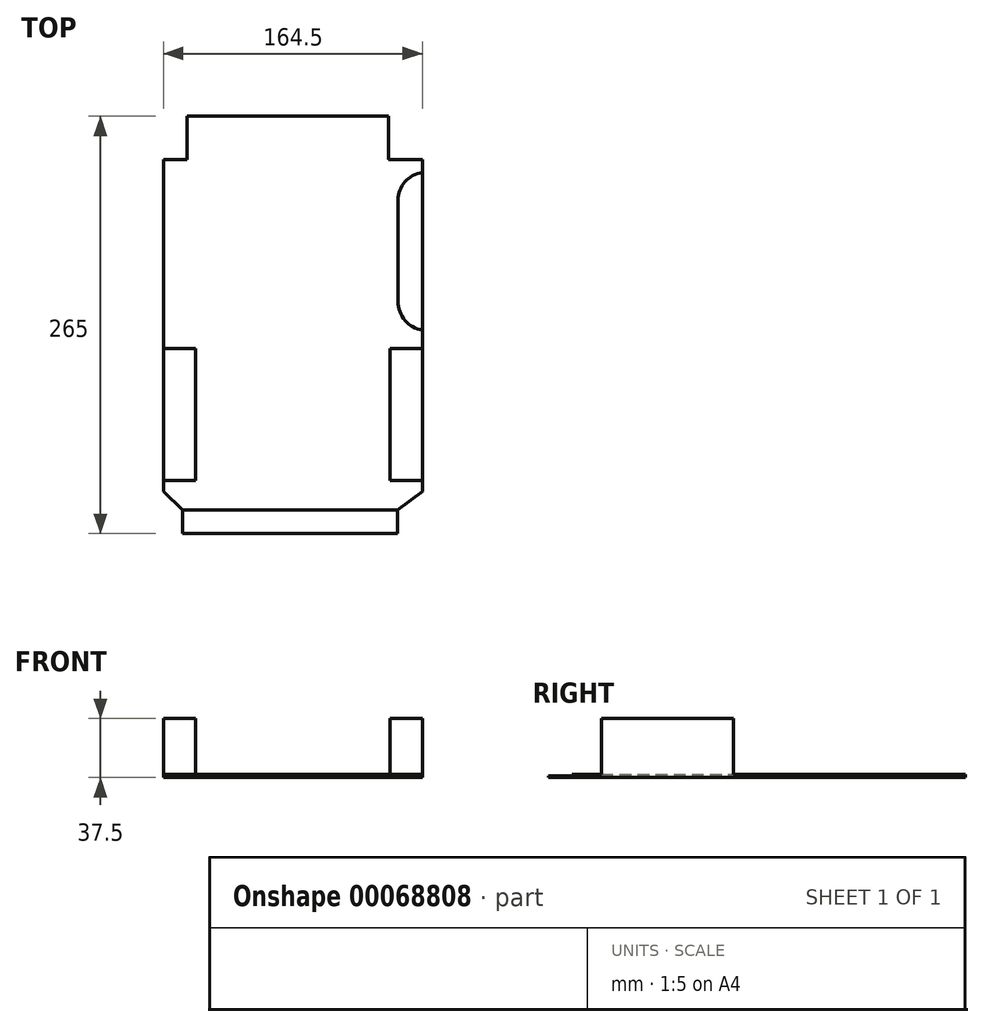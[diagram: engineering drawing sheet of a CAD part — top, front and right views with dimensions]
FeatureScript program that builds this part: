
annotation { "Feature Type Name" : "Feature", "Feature Type Description" : "" }
export const myFeature = defineFeature(function(context is Context, id is Id, definition is map)
    precondition{}
    {
        {
            var Q0;
            Q0=qCreatedBy(makeId("Top.planeOp"),FACE);
            var sketch = newSketch(context, id + "F0", { "sketchPlane" : qUnion([Q0])});
            skLineSegment(sketch, "E0", {"start": v(0, 0) * mm, "end": v(84.75, 0) * mm});
            skLineSegment(sketch, "E1", {"start": v(84.75, 0) * mm, "end": v(84.75, 15) * mm});
            skLineSegment(sketch, "E2", {"start": v(84.75, 15) * mm, "end": v(100.6, 26.65) * mm});
            skLineSegment(sketch, "E3", {"start": v(100.6, 26.65) * mm, "end": v(100.6, 33.65) * mm});
            skLineSegment(sketch, "E4", {"start": v(100.6, 33.65) * mm, "end": v(80.1, 33.65) * mm});
            skLineSegment(sketch, "E5", {"start": v(80.1, 33.65) * mm, "end": v(80.1, 117.65) * mm});
            skLineSegment(sketch, "E6", {"start": v(80.1, 117.65) * mm, "end": v(100.6, 117.65) * mm});
            skLineSegment(sketch, "E7", {"start": v(100.6, 117.65) * mm, "end": v(100.6, 129.15) * mm});
            skLineSegment(sketch, "E8", {"start": v(100.6, 129.15) * mm, "end": v(100.6, 229.15) * mm});
            skLineSegment(sketch, "E9", {"start": v(79.13, 237.55) * mm, "end": v(79.13, 265) * mm});
            skLineSegment(sketch, "E10", {"start": v(79.13, 265) * mm, "end": v(-48.95, 265) * mm});
            skLineSegment(sketch, "E11", {"start": v(-48.95, 265) * mm, "end": v(-48.95, 237.55) * mm});
            skLineSegment(sketch, "E12", {"start": v(-48.95, 237.55) * mm, "end": v(-63.9, 237.55) * mm});
            skLineSegment(sketch, "E13", {"start": v(-63.9, 237.55) * mm, "end": v(-63.9, 180.6) * mm});
            skLineSegment(sketch, "E14", {"start": v(-63.9, 180.6) * mm, "end": v(-63.9, 117.65) * mm});
            skLineSegment(sketch, "E15", {"start": v(-63.9, 117.65) * mm, "end": v(-43.4, 117.65) * mm});
            skLineSegment(sketch, "E16", {"start": v(-43.4, 117.65) * mm, "end": v(-43.4, 33.65) * mm});
            skLineSegment(sketch, "E17", {"start": v(-43.4, 33.65) * mm, "end": v(-63.9, 33.65) * mm});
            skLineSegment(sketch, "E18", {"start": v(-63.9, 33.65) * mm, "end": v(-63.9, 26.65) * mm});
            skLineSegment(sketch, "E19", {"start": v(-63.9, 26.65) * mm, "end": v(-51.75, 15) * mm});
            skLineSegment(sketch, "E20", {"start": v(-51.75, 15) * mm, "end": v(-51.75, 0) * mm});
            skLineSegment(sketch, "E21", {"start": v(-51.75, 0) * mm, "end": v(0, 0) * mm});
            skLineSegment(sketch, "E22", {"start": v(85.1, 211.82) * mm, "end": v(85.1, 147.36) * mm});
            skArc(sketch, "E23", {"start": v(100.6, 229.15) * mm, "mid": v(89.54, 223.44) * mm, "end": v(85.1, 211.82) * mm});
            skArc(sketch, "E24", {"start": v(85.1, 147.36) * mm, "mid": v(89.5, 135.4) * mm, "end": v(100.6, 129.15) * mm});
            skLineSegment(sketch, "E25", {"start": v(-51.75, 15) * mm, "end": v(84.75, 15) * mm});
            skLineSegment(sketch, "E26", {"start": v(-63.9, 117.65) * mm, "end": v(-63.9, 33.65) * mm});
            skLineSegment(sketch, "E27", {"start": v(100.6, 117.65) * mm, "end": v(100.6, 33.65) * mm});
            skLineSegment(sketch, "E28", {"start": v(79.13, 237.55) * mm, "end": v(100.6, 237.55) * mm});
            skLineSegment(sketch, "E29", {"start": v(100.6, 237.55) * mm, "end": v(100.6, 229.15) * mm});
            skSolve(sketch);
        }
        {
            var Q0;
            Q0=makeQuery(id+"F0.imprint","IMPRINT",FACE,{"disambiguationData":[TD([[makeQuery(id+"F0.imprint","IMPRINT",EDGE,{"derivedFrom":sQuery(id+"F0.wireOp",EDGE,"E2")}),1.0]])]});
            extrude(context, id + "F1", {"entities" : qUnion([Q0]), "depth" : 2 * mm});
        }
        {
            var Q0;
            Q0=makeQuery(id+"F0.imprint","IMPRINT",FACE,{"disambiguationData":[TD([[makeQuery(id+"F0.imprint","IMPRINT",EDGE,{"derivedFrom":sQuery(id+"F0.wireOp",EDGE,"E8")}),1.0]])]});
            var Q1;
            Q1=makeQuery(id+"F0.imprint","IMPRINT",FACE,{"disambiguationData":[TD([[makeQuery(id+"F0.imprint","IMPRINT",EDGE,{"derivedFrom":sQuery(id+"F0.wireOp",EDGE,"E0")}),1.0]])]});
            extrude(context, id + "F2", {"entities" : qUnion([Q0, Q1]), "operationType" : NewBodyOperationType.ADD, "depth" : 1 * mm});
        }
        {
            var Q0;
            Q0=makeQuery(id+"F0.imprint","IMPRINT",FACE,{"disambiguationData":[TD([[makeQuery(id+"F0.imprint","IMPRINT",EDGE,{"derivedFrom":sQuery(id+"F0.wireOp",EDGE,"E4")}),-1.0]])]});
            var Q1;
            Q1=makeQuery(id+"F0.imprint","IMPRINT",FACE,{"disambiguationData":[TD([[makeQuery(id+"F0.imprint","IMPRINT",EDGE,{"derivedFrom":sQuery(id+"F0.wireOp",EDGE,"E15")}),-1.0]])]});
            extrude(context, id + "F3", {"entities" : qUnion([Q0, Q1]), "operationType" : NewBodyOperationType.ADD, "depth" : 37.5 * mm});
        }
    });
